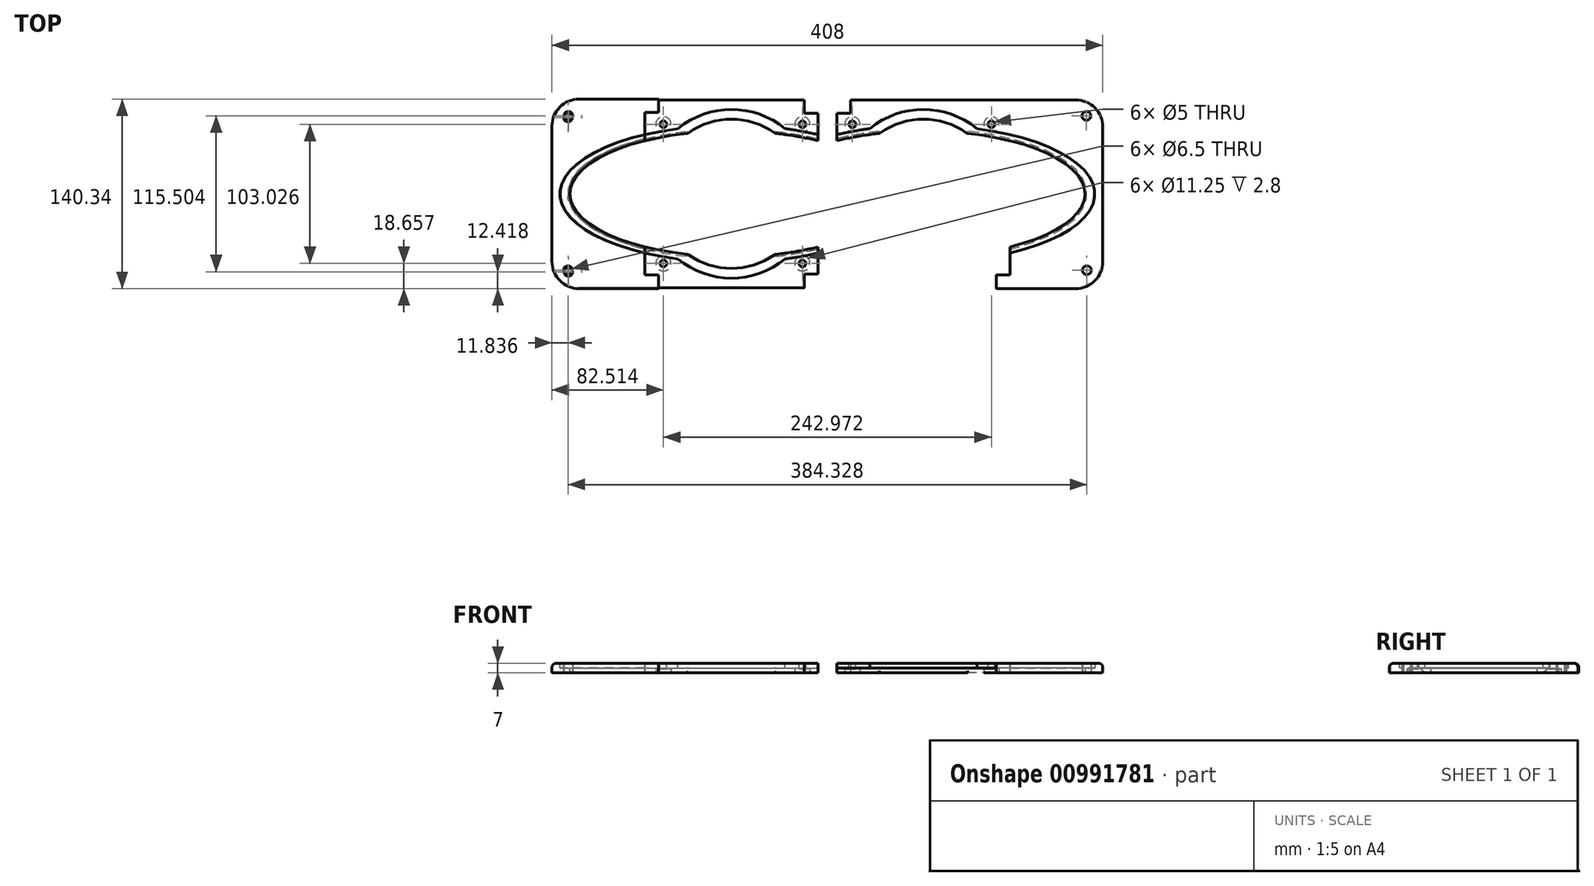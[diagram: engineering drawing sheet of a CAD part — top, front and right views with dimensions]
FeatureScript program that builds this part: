
annotation { "Feature Type Name" : "Feature", "Feature Type Description" : "" }
export const myFeature = defineFeature(function(context is Context, id is Id, definition is map)
    precondition{}
    {
        {
            var Q0;
            Q0=qCreatedBy(makeId("Top.planeOp"),FACE);
            var sketch = newSketch(context, id + "F0", { "sketchPlane" : qUnion([Q0])});
            skLineSegment(sketch, "E0.bottom", {"start": v(-62.7, 69.53) * mm, "end": v(204, 69.53) * mm});
            skLineSegment(sketch, "E0.top", {"start": v(-62.7, -70.17) * mm, "end": v(204, -70.17) * mm});
            skLineSegment(sketch, "E0.left", {"start": v(-62.7, 69.53) * mm, "end": v(-62.7, -70.17) * mm});
            skLineSegment(sketch, "E0.right", {"start": v(204, 69.53) * mm, "end": v(204, -70.17) * mm});
            skSolve(sketch);
        }
        {
            var Q0;
            Q0=qSketchRegion(id+"F0",true);
            extrude(context, id + "F1", {"entities" : qUnion([Q0]), "depth" : 7 * mm, "offsetDistance" : 25 * mm});
        }
        {
            var Q0;
            Q0=makeQuery(id+"F1.opExtrude","SWEPT_EDGE",EDGE,{"disambiguationData":[OSD([sQuery(id+"F0.wireOp",EDGE,"E0.bottom"),sQuery(id+"F0.wireOp",EDGE,"E0.left")])]});
            var Q1;
            Q1=makeQuery(id+"F1.opExtrude","SWEPT_EDGE",EDGE,{"disambiguationData":[OSD([sQuery(id+"F0.wireOp",EDGE,"E0.bottom"),sQuery(id+"F0.wireOp",EDGE,"E0.right")])]});
            var Q2;
            Q2=makeQuery(id+"F1.opExtrude","SWEPT_EDGE",EDGE,{"disambiguationData":[OSD([sQuery(id+"F0.wireOp",EDGE,"E0.top"),sQuery(id+"F0.wireOp",EDGE,"E0.left")])]});
            var Q3;
            Q3=makeQuery(id+"F1.opExtrude","SWEPT_EDGE",EDGE,{"disambiguationData":[OSD([sQuery(id+"F0.wireOp",EDGE,"E0.top"),sQuery(id+"F0.wireOp",EDGE,"E0.right")])]});
            fillet(context, id + "F2", {"entities" : qUnion([Q0, Q1, Q2, Q3]), "radius" : 20 * mm, "tangentPropagation" : true, "allowEdgeOverflow" : false});
        }
        {
            var Q0;
            Q0=makeQuery(id+"F1.opExtrude","CAP_FACE",FACE,{"disambiguationData":[OSD([sQuery(id+"F0.wireOp",EDGE,"E0.bottom"),sQuery(id+"F0.wireOp",EDGE,"E0.top"),sQuery(id+"F0.wireOp",EDGE,"E0.left"),sQuery(id+"F0.wireOp",EDGE,"E0.right")])],"isStart":false});
            var sketch = newSketch(context, id + "F3", { "sketchPlane" : qUnion([Q0])});
            skArc(sketch, "E1", {"start": v(31.34, -48.25) * mm, "mid": v(71.07, -62.5) * mm, "end": v(110.8, -48.25) * mm});
            skArc(sketch, "E2", {"start": v(38.81, -44.86) * mm, "mid": v(71.07, -55.25) * mm, "end": v(103.33, -44.86) * mm});
            skEllipticalArc(sketch, "E3", {});
            skEllipticalArc(sketch, "E4", {});
            skArc(sketch, "E5.trimOffspring", {"start": v(110.8, 48.25) * mm, "mid": v(71.07, 62.5) * mm, "end": v(31.34, 48.25) * mm});
            skArc(sketch, "E6.trimOffspring", {"start": v(103.33, 44.86) * mm, "mid": v(71.07, 55.25) * mm, "end": v(38.81, 44.86) * mm});
            skEllipticalArc(sketch, "E7.trimOffspring", {});
            skEllipticalArc(sketch, "E8.trimOffspring", {});
            const initialGuessF3  = {"E3": [0.07106995469066332, 0, 1, 0, 0.127, 0.0508, 1.8889341785773763, 4.3942511286022095], "E4": [0.07106995469066332, 0, 1, 0, 0.11970657223728468, 0.04657823190519375, 1.843644348143109, 4.439540959036477], "E7.trimOffspring": [0.07106995469066332, 0, 1, 0, 0.127, 0.0508, 5.030526832167171, 1.2526584750124172], "E8.trimOffspring": [0.07106995469066332, 0, 1, 0, 0.11970657223728468, 0.04657823190519375, 4.985237001732902, 1.2979483054466843]};
            skSetInitialGuess(sketch, initialGuessF3);
            skSolve(sketch);
        }
        {
            var Q0;
            Q0=qSketchRegion(id+"F3",true);
            extrude(context, id + "F4", {"entities" : qUnion([Q0]), "operationType" : NewBodyOperationType.REMOVE, "oppositeDirection" : true, "depth" : 3.5 * mm, "offsetDistance" : 25 * mm});
        }
        {
            var Q0;
            Q0=makeQuery(id+"F3.imprint","IMPRINT",FACE,{"disambiguationData":[TD([[makeQuery(id+"F3.imprint","IMPRINT",EDGE,{"derivedFrom":sQuery(id+"F3.wireOp",EDGE,"E2")}),1.0]])]});
            extrude(context, id + "F5", {"entities" : qUnion([Q0]), "operationType" : NewBodyOperationType.REMOVE, "oppositeDirection" : true, "depth" : 10 * mm, "offsetDistance" : 25 * mm});
        }
        {
            var Q0;
            Q0=makeQuery(id+"F1.opExtrude","CAP_FACE",FACE,{"disambiguationData":[OSD([sQuery(id+"F0.wireOp",EDGE,"E0.bottom"),sQuery(id+"F0.wireOp",EDGE,"E0.top"),sQuery(id+"F0.wireOp",EDGE,"E0.left"),sQuery(id+"F0.wireOp",EDGE,"E0.right")])],"isStart":true});
            var sketch = newSketch(context, id + "F6", { "sketchPlane" : qUnion([Q0])});
            skCircle(sketch, "E9", {"center": v(-49.54, 56.21) * mm, "radius": 3.25 * mm});
            skCircle(sketch, "E10", {"center": v(192.16, 56.56) * mm, "radius": 3.25 * mm});
            skCircle(sketch, "E11", {"center": v(191.88, -57.75) * mm, "radius": 3.25 * mm});
            skCircle(sketch, "E12", {"center": v(-49.09, -57.75) * mm, "radius": 3.25 * mm});
            skSolve(sketch);
        }
        {
            var Q0;
            Q0=makeQuery(id+"F6.imprint","IMPRINT",FACE,{"disambiguationData":[TD([[makeQuery(id+"F6.imprint","IMPRINT",EDGE,{"derivedFrom":sQuery(id+"F6.wireOp",EDGE,"E9")}),1.0]])]});
            var Q1;
            Q1=makeQuery(id+"F6.imprint","IMPRINT",FACE,{"disambiguationData":[TD([[makeQuery(id+"F6.imprint","IMPRINT",EDGE,{"derivedFrom":sQuery(id+"F6.wireOp",EDGE,"E10")}),1.0]])]});
            var Q2;
            Q2=makeQuery(id+"F6.imprint","IMPRINT",FACE,{"disambiguationData":[TD([[makeQuery(id+"F6.imprint","IMPRINT",EDGE,{"derivedFrom":sQuery(id+"F6.wireOp",EDGE,"E11")}),1.0]])]});
            var Q3;
            Q3=makeQuery(id+"F6.imprint","IMPRINT",FACE,{"disambiguationData":[TD([[makeQuery(id+"F6.imprint","IMPRINT",EDGE,{"derivedFrom":sQuery(id+"F6.wireOp",EDGE,"E12")}),1.0]])]});
            extrude(context, id + "F7", {"entities" : qUnion([Q0, Q1, Q2, Q3]), "operationType" : NewBodyOperationType.REMOVE, "oppositeDirection" : true, "depth" : 8 * mm, "offsetDistance" : 25 * mm});
        }
        {
            var Q0;
            {var subQ0=sQuery(id+"F0.wireOp",EDGE,"E0.left");var subQ1=sQuery(id+"F0.wireOp",EDGE,"E0.bottom");var subQ2=sQuery(id+"F0.wireOp",EDGE,"E0.top");var subQ3=sQuery(id+"F0.wireOp",EDGE,"E0.right");Q0=makeQuery(id+"F4.boolean.opBoolean","SPLIT",FACE,{"disambiguationData":[TD([makeQuery(id+"F1.opExtrude","SWEPT_FACE",FACE,{"disambiguationData":[OSD([subQ1])]})])],"derivedFrom":makeQuery(id+"F1.opExtrude","CAP_FACE",FACE,{"disambiguationData":[OSD([subQ1,subQ2,subQ0,subQ3])],"isStart":false})});}
            var sketch = newSketch(context, id + "F8", { "sketchPlane" : qUnion([Q0])});
            skCircle(sketch, "E13", {"center": v(18.49, 51.51) * mm, "radius": 2.5 * mm});
            skCircle(sketch, "E14", {"center": v(121.49, 51.51) * mm, "radius": 2.5 * mm});
            skCircle(sketch, "E15", {"center": v(121.49, -51.49) * mm, "radius": 2.5 * mm});
            skCircle(sketch, "E16", {"center": v(18.49, -51.49) * mm, "radius": 2.5 * mm});
            skSolve(sketch);
        }
        {
            var Q0;
            Q0=qSketchRegion(id+"F8",true);
            extrude(context, id + "F9", {"entities" : qUnion([Q0]), "operationType" : NewBodyOperationType.REMOVE, "oppositeDirection" : true, "depth" : 8 * mm, "offsetDistance" : 25 * mm});
        }
        {
            var Q0;
            Q0=makeQuery(id+"F1.opExtrude","CAP_FACE",FACE,{"disambiguationData":[OSD([sQuery(id+"F0.wireOp",EDGE,"E0.bottom"),sQuery(id+"F0.wireOp",EDGE,"E0.top"),sQuery(id+"F0.wireOp",EDGE,"E0.left"),sQuery(id+"F0.wireOp",EDGE,"E0.right")])],"isStart":true});
            var sketch = newSketch(context, id + "F10", { "sketchPlane" : qUnion([Q0])});
            skCircle(sketch, "E17", {"center": v(18.49, 51.49) * mm, "radius": 5.62 * mm});
            skCircle(sketch, "E18", {"center": v(121.49, 51.49) * mm, "radius": 5.62 * mm});
            skCircle(sketch, "E19", {"center": v(121.49, -51.51) * mm, "radius": 5.62 * mm});
            skCircle(sketch, "E20", {"center": v(18.49, -51.51) * mm, "radius": 5.62 * mm});
            skSolve(sketch);
        }
        {
            var Q0;
            Q0=qSketchRegion(id+"F10",true);
            extrude(context, id + "F11", {"entities" : qUnion([Q0]), "operationType" : NewBodyOperationType.REMOVE, "oppositeDirection" : true, "depth" : 2.8 * mm, "offsetDistance" : 25 * mm});
        }
        {
            var Q0;
            Q0=makeQuery(id+"F5.boolean.opBoolean","INTERSECT",EDGE,{"derivedFrom":[makeQuery(id+"F1.opExtrude","CAP_FACE",FACE,{"disambiguationData":[OSD([sQuery(id+"F0.wireOp",EDGE,"E0.bottom"),sQuery(id+"F0.wireOp",EDGE,"E0.top"),sQuery(id+"F0.wireOp",EDGE,"E0.left"),sQuery(id+"F0.wireOp",EDGE,"E0.right")])],"isStart":true}),makeQuery(id+"F5.opExtrude","SWEPT_FACE",FACE,{"disambiguationData":[OSD([sQuery(id+"F3.wireOp",EDGE,"E2")])]})]});
            fillet(context, id + "F12", {"entities" : qUnion([Q0]), "radius" : 1.5 * mm, "tangentPropagation" : true, "allowEdgeOverflow" : false});
        }
        {
            var Q0;
            Q0=makeQuery(id+"F1.opExtrude","CAP_EDGE",EDGE,{"disambiguationData":[OSD([sQuery(id+"F0.wireOp",EDGE,"E0.bottom")])],"isStart":false});
            fillet(context, id + "F13", {"entities" : qUnion([Q0]), "radius" : 3 * mm, "tangentPropagation" : true, "allowEdgeOverflow" : false});
        }
        {
            var Q0;
            Q0=makeQuery(id+"F5.boolean.opBoolean","INTERSECT",EDGE,{"derivedFrom":[makeQuery(id+"F1.opExtrude","CAP_FACE",FACE,{"disambiguationData":[OSD([sQuery(id+"F0.wireOp",EDGE,"E0.bottom"),sQuery(id+"F0.wireOp",EDGE,"E0.top"),sQuery(id+"F0.wireOp",EDGE,"E0.left"),sQuery(id+"F0.wireOp",EDGE,"E0.right")])],"isStart":true}),makeQuery(id+"F5.opExtrude","SWEPT_FACE",FACE,{"disambiguationData":[OSD([sQuery(id+"F3.wireOp",EDGE,"E4")])]})]});
            var Q1;
            Q1=makeQuery(id+"F5.boolean.opBoolean","INTERSECT",EDGE,{"derivedFrom":[makeQuery(id+"F1.opExtrude","CAP_FACE",FACE,{"disambiguationData":[OSD([sQuery(id+"F0.wireOp",EDGE,"E0.bottom"),sQuery(id+"F0.wireOp",EDGE,"E0.top"),sQuery(id+"F0.wireOp",EDGE,"E0.left"),sQuery(id+"F0.wireOp",EDGE,"E0.right")])],"isStart":true}),makeQuery(id+"F5.opExtrude","SWEPT_FACE",FACE,{"disambiguationData":[OSD([sQuery(id+"F3.wireOp",EDGE,"E8.trimOffspring")])]})]});
            fillet(context, id + "F14", {"entities" : qUnion([Q0, Q1]), "radius" : 1.5 * mm, "tangentPropagation" : true, "allowEdgeOverflow" : false});
        }
        {
            var Q0;
            Q0=makeQuery(id+"F5.boolean.opBoolean","INTERSECT",EDGE,{"derivedFrom":[makeQuery(id+"F1.opExtrude","CAP_FACE",FACE,{"disambiguationData":[OSD([sQuery(id+"F0.wireOp",EDGE,"E0.bottom"),sQuery(id+"F0.wireOp",EDGE,"E0.top"),sQuery(id+"F0.wireOp",EDGE,"E0.left"),sQuery(id+"F0.wireOp",EDGE,"E0.right")])],"isStart":true}),makeQuery(id+"F5.opExtrude","SWEPT_FACE",FACE,{"disambiguationData":[OSD([sQuery(id+"F3.wireOp",EDGE,"E6.trimOffspring")])]})]});
            fillet(context, id + "F15", {"entities" : qUnion([Q0]), "radius" : 1.5 * mm, "tangentPropagation" : true, "allowEdgeOverflow" : false});
        }
        {
            var Q0;
            Q0=qCreatedBy(makeId("Top.planeOp"),FACE);
            var sketch = newSketch(context, id + "F16", { "sketchPlane" : qUnion([Q0])});
            skLineSegment(sketch, "E21", {"start": v(71.07, -55.25) * mm, "end": v(71.07, 55.25) * mm, "construction": true});
            skLineSegment(sketch, "E22", {"start": v(-48.64, 0) * mm, "end": v(190.78, 0) * mm, "construction": true});
            skLineSegment(sketch, "E23", {"start": v(7, 59.53) * mm, "end": v(7, 0) * mm});
            skLineSegment(sketch, "E24", {"start": v(7, 0) * mm, "end": v(135.14, 0) * mm});
            skLineSegment(sketch, "E25", {"start": v(135.14, 0) * mm, "end": v(135.14, -60.17) * mm});
            skLineSegment(sketch, "E26", {"start": v(7, 59.53) * mm, "end": v(17, 59.53) * mm});
            skLineSegment(sketch, "E27", {"start": v(17, 59.53) * mm, "end": v(17, 69.53) * mm});
            skLineSegment(sketch, "E28", {"start": v(17, 69.53) * mm, "end": v(-72.19, 69.53) * mm});
            skLineSegment(sketch, "E29", {"start": v(-72.19, 69.53) * mm, "end": v(-72.19, -70.17) * mm});
            skLineSegment(sketch, "E30", {"start": v(-72.19, -70.17) * mm, "end": v(125.14, -70.17) * mm});
            skLineSegment(sketch, "E31", {"start": v(135.14, -60.17) * mm, "end": v(125.14, -60.17) * mm});
            skLineSegment(sketch, "E32", {"start": v(125.14, -60.17) * mm, "end": v(125.14, -70.17) * mm});
            skPoint(sketch, "E33.orphan", {"position": v(135.14, -70.17) * mm});
            skSolve(sketch);
        }
        {
            var Q0;
            Q0=makeQuery(id+"F16.imprint","IMPRINT",FACE,{"disambiguationData":[TD([[makeQuery(id+"F16.imprint","IMPRINT",EDGE,{"derivedFrom":sQuery(id+"F16.wireOp",EDGE,"E23")}),-1.0]])]});
            extrude(context, id + "F17", {"entities" : qUnion([Q0]), "operationType" : NewBodyOperationType.REMOVE, "depth" : 54.1 * mm, "offsetDistance" : 25 * mm});
        }
        {
            var Q0;
            Q0=qCreatedBy(makeId("Front.planeOp"),FACE);
            var sketch = newSketch(context, id + "F18", { "sketchPlane" : qUnion([Q0])});
            skLineSegment(sketch, "E34", {"start": v(71.07, 88.7) * mm, "end": v(71.07, 7) * mm, "construction": true});
            skSolve(sketch);
        }
        {
            var Q0;
            Q0=makeQuery(id+"F1.opExtrude","SWEPT_BODY",BODY,{"disambiguationData":[OSD([sQuery(id+"F0.wireOp",EDGE,"E0.bottom"),sQuery(id+"F0.wireOp",EDGE,"E0.top"),sQuery(id+"F0.wireOp",EDGE,"E0.left"),sQuery(id+"F0.wireOp",EDGE,"E0.right")])]});
            var Q1;
            Q1=qCreatedBy(makeId("Right.planeOp"),FACE);
            mirror(context, id + "F19", {"entities" : qUnion([Q0]), "mirrorPlane" : qUnion([Q1])});
        }
        {
            var Q0;
            Q0=makeQuery(id+"F19.opPattern","COPY",BODY,{"derivedFrom":makeQuery(id+"F1.opExtrude","SWEPT_BODY",BODY,{"disambiguationData":[OSD([sQuery(id+"F0.wireOp",EDGE,"E0.bottom"),sQuery(id+"F0.wireOp",EDGE,"E0.top"),sQuery(id+"F0.wireOp",EDGE,"E0.left"),sQuery(id+"F0.wireOp",EDGE,"E0.right")])]}),"instanceName":"1"});
            var Q1;
            Q1=qCreatedBy(makeId("Front.planeOp"),FACE);
            mirror(context, id + "F20", {"entities" : qUnion([Q0]), "mirrorPlane" : qUnion([Q1])});
        }
    });
